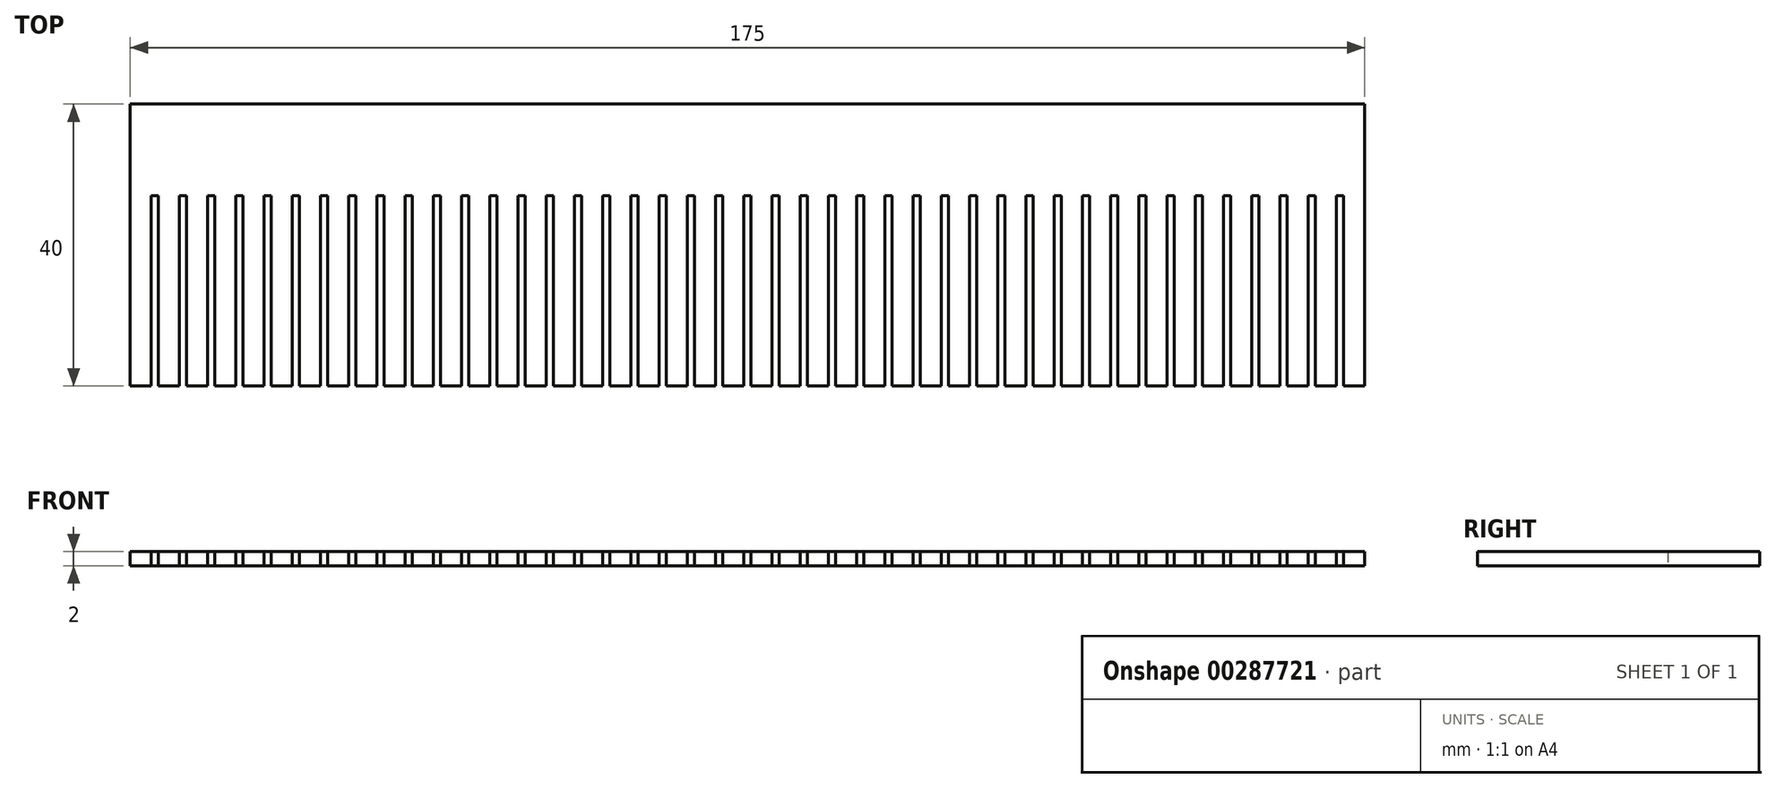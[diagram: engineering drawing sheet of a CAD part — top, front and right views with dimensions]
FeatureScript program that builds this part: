
annotation { "Feature Type Name" : "Feature", "Feature Type Description" : "" }
export const myFeature = defineFeature(function(context is Context, id is Id, definition is map)
    precondition{}
    {
        {
            var Q0;
            Q0=qCreatedBy(makeId("Top.planeOp"),FACE);
            var sketch = newSketch(context, id + "F0", { "sketchPlane" : qUnion([Q0])});
            skLineSegment(sketch, "E0", {"start": v(-88.37, 37.55) * mm, "end": v(86.63, 37.55) * mm});
            skLineSegment(sketch, "E1", {"start": v(-88.37, 37.55) * mm, "end": v(-88.37, 24.55) * mm});
            skLineSegment(sketch, "E2", {"start": v(-88.37, 24.55) * mm, "end": v(86.63, 24.55) * mm});
            skLineSegment(sketch, "E3", {"start": v(86.63, 24.55) * mm, "end": v(86.63, 37.55) * mm});
            skLineSegment(sketch, "E4", {"start": v(-88.37, 24.55) * mm, "end": v(-88.37, -2.45) * mm});
            skLineSegment(sketch, "E5", {"start": v(-88.37, -2.45) * mm, "end": v(-85.37, -2.45) * mm});
            skLineSegment(sketch, "E6", {"start": v(-85.37, -2.45) * mm, "end": v(-85.37, 24.55) * mm});
            skLineSegment(sketch, "E7.1.0.0", {"start": v(-81.37, -2.45) * mm, "end": v(-81.37, 24.55) * mm});
            skLineSegment(sketch, "E7.1.0.1", {"start": v(-84.37, 24.55) * mm, "end": v(-84.37, -2.45) * mm});
            skLineSegment(sketch, "E7.1.0.2", {"start": v(-84.37, -2.45) * mm, "end": v(-81.37, -2.45) * mm});
            skLineSegment(sketch, "E7.2.0.0", {"start": v(-77.37, -2.45) * mm, "end": v(-77.37, 24.55) * mm});
            skLineSegment(sketch, "E7.2.0.1", {"start": v(-80.37, 24.55) * mm, "end": v(-80.37, -2.45) * mm});
            skLineSegment(sketch, "E7.2.0.2", {"start": v(-80.37, -2.45) * mm, "end": v(-77.37, -2.45) * mm});
            skLineSegment(sketch, "E7.3.0.0", {"start": v(-73.37, -2.45) * mm, "end": v(-73.37, 24.55) * mm});
            skLineSegment(sketch, "E7.3.0.1", {"start": v(-76.37, 24.55) * mm, "end": v(-76.37, -2.45) * mm});
            skLineSegment(sketch, "E7.3.0.2", {"start": v(-76.37, -2.45) * mm, "end": v(-73.37, -2.45) * mm});
            skLineSegment(sketch, "E7.4.0.0", {"start": v(-69.37, -2.45) * mm, "end": v(-69.37, 24.55) * mm});
            skLineSegment(sketch, "E7.4.0.1", {"start": v(-72.37, 24.55) * mm, "end": v(-72.37, -2.45) * mm});
            skLineSegment(sketch, "E7.4.0.2", {"start": v(-72.37, -2.45) * mm, "end": v(-69.37, -2.45) * mm});
            skLineSegment(sketch, "E7.5.0.0", {"start": v(-65.37, -2.45) * mm, "end": v(-65.37, 24.55) * mm});
            skLineSegment(sketch, "E7.5.0.1", {"start": v(-68.37, 24.55) * mm, "end": v(-68.37, -2.45) * mm});
            skLineSegment(sketch, "E7.5.0.2", {"start": v(-68.37, -2.45) * mm, "end": v(-65.37, -2.45) * mm});
            skLineSegment(sketch, "E7.6.0.0", {"start": v(-61.37, -2.45) * mm, "end": v(-61.37, 24.55) * mm});
            skLineSegment(sketch, "E7.6.0.1", {"start": v(-64.37, 24.55) * mm, "end": v(-64.37, -2.45) * mm});
            skLineSegment(sketch, "E7.6.0.2", {"start": v(-64.37, -2.45) * mm, "end": v(-61.37, -2.45) * mm});
            skLineSegment(sketch, "E7.7.0.0", {"start": v(-57.37, -2.45) * mm, "end": v(-57.37, 24.55) * mm});
            skLineSegment(sketch, "E7.7.0.1", {"start": v(-60.37, 24.55) * mm, "end": v(-60.37, -2.45) * mm});
            skLineSegment(sketch, "E7.7.0.2", {"start": v(-60.37, -2.45) * mm, "end": v(-57.37, -2.45) * mm});
            skLineSegment(sketch, "E7.8.0.0", {"start": v(-53.37, -2.45) * mm, "end": v(-53.37, 24.55) * mm});
            skLineSegment(sketch, "E7.8.0.1", {"start": v(-56.37, 24.55) * mm, "end": v(-56.37, -2.45) * mm});
            skLineSegment(sketch, "E7.8.0.2", {"start": v(-56.37, -2.45) * mm, "end": v(-53.37, -2.45) * mm});
            skLineSegment(sketch, "E7.9.0.0", {"start": v(-49.37, -2.45) * mm, "end": v(-49.37, 24.55) * mm});
            skLineSegment(sketch, "E7.9.0.1", {"start": v(-52.37, 24.55) * mm, "end": v(-52.37, -2.45) * mm});
            skLineSegment(sketch, "E7.9.0.2", {"start": v(-52.37, -2.45) * mm, "end": v(-49.37, -2.45) * mm});
            skLineSegment(sketch, "E7.10.0.0", {"start": v(-45.37, -2.45) * mm, "end": v(-45.37, 24.55) * mm});
            skLineSegment(sketch, "E7.10.0.1", {"start": v(-48.37, 24.55) * mm, "end": v(-48.37, -2.45) * mm});
            skLineSegment(sketch, "E7.10.0.2", {"start": v(-48.37, -2.45) * mm, "end": v(-45.37, -2.45) * mm});
            skLineSegment(sketch, "E7.11.0.0", {"start": v(-41.37, -2.45) * mm, "end": v(-41.37, 24.55) * mm});
            skLineSegment(sketch, "E7.11.0.1", {"start": v(-44.37, 24.55) * mm, "end": v(-44.37, -2.45) * mm});
            skLineSegment(sketch, "E7.11.0.2", {"start": v(-44.37, -2.45) * mm, "end": v(-41.37, -2.45) * mm});
            skLineSegment(sketch, "E7.12.0.0", {"start": v(-37.37, -2.45) * mm, "end": v(-37.37, 24.55) * mm});
            skLineSegment(sketch, "E7.12.0.1", {"start": v(-40.37, 24.55) * mm, "end": v(-40.37, -2.45) * mm});
            skLineSegment(sketch, "E7.12.0.2", {"start": v(-40.37, -2.45) * mm, "end": v(-37.37, -2.45) * mm});
            skLineSegment(sketch, "E7.13.0.0", {"start": v(-33.37, -2.45) * mm, "end": v(-33.37, 24.55) * mm});
            skLineSegment(sketch, "E7.13.0.1", {"start": v(-36.37, 24.55) * mm, "end": v(-36.37, -2.45) * mm});
            skLineSegment(sketch, "E7.13.0.2", {"start": v(-36.37, -2.45) * mm, "end": v(-33.37, -2.45) * mm});
            skLineSegment(sketch, "E7.14.0.0", {"start": v(-29.37, -2.45) * mm, "end": v(-29.37, 24.55) * mm});
            skLineSegment(sketch, "E7.14.0.1", {"start": v(-32.37, 24.55) * mm, "end": v(-32.37, -2.45) * mm});
            skLineSegment(sketch, "E7.14.0.2", {"start": v(-32.37, -2.45) * mm, "end": v(-29.37, -2.45) * mm});
            skLineSegment(sketch, "E7.15.0.0", {"start": v(-25.37, -2.45) * mm, "end": v(-25.37, 24.55) * mm});
            skLineSegment(sketch, "E7.15.0.1", {"start": v(-28.37, 24.55) * mm, "end": v(-28.37, -2.45) * mm});
            skLineSegment(sketch, "E7.15.0.2", {"start": v(-28.37, -2.45) * mm, "end": v(-25.37, -2.45) * mm});
            skLineSegment(sketch, "E7.16.0.0", {"start": v(-21.37, -2.45) * mm, "end": v(-21.37, 24.55) * mm});
            skLineSegment(sketch, "E7.16.0.1", {"start": v(-24.37, 24.55) * mm, "end": v(-24.37, -2.45) * mm});
            skLineSegment(sketch, "E7.16.0.2", {"start": v(-24.37, -2.45) * mm, "end": v(-21.37, -2.45) * mm});
            skLineSegment(sketch, "E7.17.0.0", {"start": v(-17.37, -2.45) * mm, "end": v(-17.37, 24.55) * mm});
            skLineSegment(sketch, "E7.17.0.1", {"start": v(-20.37, 24.55) * mm, "end": v(-20.37, -2.45) * mm});
            skLineSegment(sketch, "E7.17.0.2", {"start": v(-20.37, -2.45) * mm, "end": v(-17.37, -2.45) * mm});
            skLineSegment(sketch, "E7.18.0.0", {"start": v(-13.37, -2.45) * mm, "end": v(-13.37, 24.55) * mm});
            skLineSegment(sketch, "E7.18.0.1", {"start": v(-16.37, 24.55) * mm, "end": v(-16.37, -2.45) * mm});
            skLineSegment(sketch, "E7.18.0.2", {"start": v(-16.37, -2.45) * mm, "end": v(-13.37, -2.45) * mm});
            skLineSegment(sketch, "E7.19.0.0", {"start": v(-9.37, -2.45) * mm, "end": v(-9.37, 24.55) * mm});
            skLineSegment(sketch, "E7.19.0.1", {"start": v(-12.37, 24.55) * mm, "end": v(-12.37, -2.45) * mm});
            skLineSegment(sketch, "E7.19.0.2", {"start": v(-12.37, -2.45) * mm, "end": v(-9.37, -2.45) * mm});
            skLineSegment(sketch, "E7.20.0.0", {"start": v(-5.37, -2.45) * mm, "end": v(-5.37, 24.55) * mm});
            skLineSegment(sketch, "E7.20.0.1", {"start": v(-8.37, 24.55) * mm, "end": v(-8.37, -2.45) * mm});
            skLineSegment(sketch, "E7.20.0.2", {"start": v(-8.37, -2.45) * mm, "end": v(-5.37, -2.45) * mm});
            skLineSegment(sketch, "E7.21.0.0", {"start": v(-1.37, -2.45) * mm, "end": v(-1.37, 24.55) * mm});
            skLineSegment(sketch, "E7.21.0.1", {"start": v(-4.37, 24.55) * mm, "end": v(-4.37, -2.45) * mm});
            skLineSegment(sketch, "E7.21.0.2", {"start": v(-4.37, -2.45) * mm, "end": v(-1.37, -2.45) * mm});
            skLineSegment(sketch, "E7.22.0.0", {"start": v(2.63, -2.45) * mm, "end": v(2.63, 24.55) * mm});
            skLineSegment(sketch, "E7.22.0.1", {"start": v(-0.37, 24.55) * mm, "end": v(-0.37, -2.45) * mm});
            skLineSegment(sketch, "E7.22.0.2", {"start": v(-0.37, -2.45) * mm, "end": v(2.63, -2.45) * mm});
            skLineSegment(sketch, "E7.23.0.0", {"start": v(6.63, -2.45) * mm, "end": v(6.63, 24.55) * mm});
            skLineSegment(sketch, "E7.23.0.1", {"start": v(3.63, 24.55) * mm, "end": v(3.63, -2.45) * mm});
            skLineSegment(sketch, "E7.23.0.2", {"start": v(3.63, -2.45) * mm, "end": v(6.63, -2.45) * mm});
            skLineSegment(sketch, "E7.24.0.0", {"start": v(10.63, -2.45) * mm, "end": v(10.63, 24.55) * mm});
            skLineSegment(sketch, "E7.24.0.1", {"start": v(7.63, 24.55) * mm, "end": v(7.63, -2.45) * mm});
            skLineSegment(sketch, "E7.24.0.2", {"start": v(7.63, -2.45) * mm, "end": v(10.63, -2.45) * mm});
            skLineSegment(sketch, "E7.25.0.0", {"start": v(14.63, -2.45) * mm, "end": v(14.63, 24.55) * mm});
            skLineSegment(sketch, "E7.25.0.1", {"start": v(11.63, 24.55) * mm, "end": v(11.63, -2.45) * mm});
            skLineSegment(sketch, "E7.25.0.2", {"start": v(11.63, -2.45) * mm, "end": v(14.63, -2.45) * mm});
            skLineSegment(sketch, "E7.26.0.0", {"start": v(18.63, -2.45) * mm, "end": v(18.63, 24.55) * mm});
            skLineSegment(sketch, "E7.26.0.1", {"start": v(15.63, 24.55) * mm, "end": v(15.63, -2.45) * mm});
            skLineSegment(sketch, "E7.26.0.2", {"start": v(15.63, -2.45) * mm, "end": v(18.63, -2.45) * mm});
            skLineSegment(sketch, "E7.27.0.0", {"start": v(22.63, -2.45) * mm, "end": v(22.63, 24.55) * mm});
            skLineSegment(sketch, "E7.27.0.1", {"start": v(19.63, 24.55) * mm, "end": v(19.63, -2.45) * mm});
            skLineSegment(sketch, "E7.27.0.2", {"start": v(19.63, -2.45) * mm, "end": v(22.63, -2.45) * mm});
            skLineSegment(sketch, "E7.28.0.0", {"start": v(26.63, -2.45) * mm, "end": v(26.63, 24.55) * mm});
            skLineSegment(sketch, "E7.28.0.1", {"start": v(23.63, 24.55) * mm, "end": v(23.63, -2.45) * mm});
            skLineSegment(sketch, "E7.28.0.2", {"start": v(23.63, -2.45) * mm, "end": v(26.63, -2.45) * mm});
            skLineSegment(sketch, "E7.29.0.0", {"start": v(30.63, -2.45) * mm, "end": v(30.63, 24.55) * mm});
            skLineSegment(sketch, "E7.29.0.1", {"start": v(27.63, 24.55) * mm, "end": v(27.63, -2.45) * mm});
            skLineSegment(sketch, "E7.29.0.2", {"start": v(27.63, -2.45) * mm, "end": v(30.63, -2.45) * mm});
            skLineSegment(sketch, "E7.30.0.0", {"start": v(34.63, -2.45) * mm, "end": v(34.63, 24.55) * mm});
            skLineSegment(sketch, "E7.30.0.1", {"start": v(31.63, 24.55) * mm, "end": v(31.63, -2.45) * mm});
            skLineSegment(sketch, "E7.30.0.2", {"start": v(31.63, -2.45) * mm, "end": v(34.63, -2.45) * mm});
            skLineSegment(sketch, "E7.31.0.0", {"start": v(38.63, -2.45) * mm, "end": v(38.63, 24.55) * mm});
            skLineSegment(sketch, "E7.31.0.1", {"start": v(35.63, 24.55) * mm, "end": v(35.63, -2.45) * mm});
            skLineSegment(sketch, "E7.31.0.2", {"start": v(35.63, -2.45) * mm, "end": v(38.63, -2.45) * mm});
            skLineSegment(sketch, "E7.32.0.0", {"start": v(42.63, -2.45) * mm, "end": v(42.63, 24.55) * mm});
            skLineSegment(sketch, "E7.32.0.1", {"start": v(39.63, 24.55) * mm, "end": v(39.63, -2.45) * mm});
            skLineSegment(sketch, "E7.32.0.2", {"start": v(39.63, -2.45) * mm, "end": v(42.63, -2.45) * mm});
            skLineSegment(sketch, "E7.33.0.0", {"start": v(46.63, -2.45) * mm, "end": v(46.63, 24.55) * mm});
            skLineSegment(sketch, "E7.33.0.1", {"start": v(43.63, 24.55) * mm, "end": v(43.63, -2.45) * mm});
            skLineSegment(sketch, "E7.33.0.2", {"start": v(43.63, -2.45) * mm, "end": v(46.63, -2.45) * mm});
            skLineSegment(sketch, "E7.34.0.0", {"start": v(50.63, -2.45) * mm, "end": v(50.63, 24.55) * mm});
            skLineSegment(sketch, "E7.34.0.1", {"start": v(47.63, 24.55) * mm, "end": v(47.63, -2.45) * mm});
            skLineSegment(sketch, "E7.34.0.2", {"start": v(47.63, -2.45) * mm, "end": v(50.63, -2.45) * mm});
            skLineSegment(sketch, "E7.35.0.0", {"start": v(54.63, -2.45) * mm, "end": v(54.63, 24.55) * mm});
            skLineSegment(sketch, "E7.35.0.1", {"start": v(51.63, 24.55) * mm, "end": v(51.63, -2.45) * mm});
            skLineSegment(sketch, "E7.35.0.2", {"start": v(51.63, -2.45) * mm, "end": v(54.63, -2.45) * mm});
            skLineSegment(sketch, "E7.36.0.0", {"start": v(58.63, -2.45) * mm, "end": v(58.63, 24.55) * mm});
            skLineSegment(sketch, "E7.36.0.1", {"start": v(55.63, 24.55) * mm, "end": v(55.63, -2.45) * mm});
            skLineSegment(sketch, "E7.36.0.2", {"start": v(55.63, -2.45) * mm, "end": v(58.63, -2.45) * mm});
            skLineSegment(sketch, "E7.37.0.0", {"start": v(62.63, -2.45) * mm, "end": v(62.63, 24.55) * mm});
            skLineSegment(sketch, "E7.37.0.1", {"start": v(59.63, 24.55) * mm, "end": v(59.63, -2.45) * mm});
            skLineSegment(sketch, "E7.37.0.2", {"start": v(59.63, -2.45) * mm, "end": v(62.63, -2.45) * mm});
            skLineSegment(sketch, "E7.38.0.0", {"start": v(66.63, -2.45) * mm, "end": v(66.63, 24.55) * mm});
            skLineSegment(sketch, "E7.38.0.1", {"start": v(63.63, 24.55) * mm, "end": v(63.63, -2.45) * mm});
            skLineSegment(sketch, "E7.38.0.2", {"start": v(63.63, -2.45) * mm, "end": v(66.63, -2.45) * mm});
            skLineSegment(sketch, "E7.39.0.0", {"start": v(70.63, -2.45) * mm, "end": v(70.63, 24.55) * mm});
            skLineSegment(sketch, "E7.39.0.1", {"start": v(67.63, 24.55) * mm, "end": v(67.63, -2.45) * mm});
            skLineSegment(sketch, "E7.39.0.2", {"start": v(67.63, -2.45) * mm, "end": v(70.63, -2.45) * mm});
            skLineSegment(sketch, "E7.40.0.0", {"start": v(74.63, -2.45) * mm, "end": v(74.63, 24.55) * mm});
            skLineSegment(sketch, "E7.40.0.1", {"start": v(71.63, 24.55) * mm, "end": v(71.63, -2.45) * mm});
            skLineSegment(sketch, "E7.40.0.2", {"start": v(71.63, -2.45) * mm, "end": v(74.63, -2.45) * mm});
            skLineSegment(sketch, "E7.41.0.0", {"start": v(78.63, -2.45) * mm, "end": v(78.63, 24.55) * mm});
            skLineSegment(sketch, "E7.41.0.1", {"start": v(75.63, 24.55) * mm, "end": v(75.63, -2.45) * mm});
            skLineSegment(sketch, "E7.41.0.2", {"start": v(75.63, -2.45) * mm, "end": v(78.63, -2.45) * mm});
            skLineSegment(sketch, "E7.42.0.0", {"start": v(82.63, -2.45) * mm, "end": v(82.63, 24.55) * mm});
            skLineSegment(sketch, "E7.42.0.1", {"start": v(79.63, 24.55) * mm, "end": v(79.63, -2.45) * mm});
            skLineSegment(sketch, "E7.42.0.2", {"start": v(79.63, -2.45) * mm, "end": v(82.63, -2.45) * mm});
            skLineSegment(sketch, "E7.43.0.0", {"start": v(86.63, -2.45) * mm, "end": v(86.63, 24.55) * mm});
            skLineSegment(sketch, "E7.43.0.1", {"start": v(83.63, 24.55) * mm, "end": v(83.63, -2.45) * mm});
            skLineSegment(sketch, "E7.43.0.2", {"start": v(83.63, -2.45) * mm, "end": v(86.63, -2.45) * mm});
            skLineSegment(sketch, "E7.direction1", {"start": v(-85.37, -2.45) * mm, "end": v(-81.37, -2.45) * mm, "construction": true});
            skSolve(sketch);
        }
        {
            var Q0;
            {var subQ0=sQuery(id+"F0.wireOp",EDGE,"E4");Q0=makeQuery(id+"F0.imprint","IMPRINT",FACE,{"disambiguationData":[TD([[makeQuery(id+"F0.imprint","IMPRINT",EDGE,{"derivedFrom":subQ0}),1.0]])]});}
            var Q1;
            {var subQ0=sQuery(id+"F0.wireOp",EDGE,"E7.1.0.0");Q1=makeQuery(id+"F0.imprint","IMPRINT",FACE,{"disambiguationData":[TD([[makeQuery(id+"F0.imprint","IMPRINT",EDGE,{"derivedFrom":subQ0}),1.0]])]});}
            var Q2;
            {var subQ0=sQuery(id+"F0.wireOp",EDGE,"E7.2.0.0");Q2=makeQuery(id+"F0.imprint","IMPRINT",FACE,{"disambiguationData":[TD([[makeQuery(id+"F0.imprint","IMPRINT",EDGE,{"derivedFrom":subQ0}),1.0]])]});}
            var Q3;
            {var subQ0=sQuery(id+"F0.wireOp",EDGE,"E7.3.0.0");Q3=makeQuery(id+"F0.imprint","IMPRINT",FACE,{"disambiguationData":[TD([[makeQuery(id+"F0.imprint","IMPRINT",EDGE,{"derivedFrom":subQ0}),1.0]])]});}
            var Q4;
            {var subQ0=sQuery(id+"F0.wireOp",EDGE,"E7.4.0.0");Q4=makeQuery(id+"F0.imprint","IMPRINT",FACE,{"disambiguationData":[TD([[makeQuery(id+"F0.imprint","IMPRINT",EDGE,{"derivedFrom":subQ0}),1.0]])]});}
            var Q5;
            {var subQ0=sQuery(id+"F0.wireOp",EDGE,"E7.5.0.0");Q5=makeQuery(id+"F0.imprint","IMPRINT",FACE,{"disambiguationData":[TD([[makeQuery(id+"F0.imprint","IMPRINT",EDGE,{"derivedFrom":subQ0}),1.0]])]});}
            var Q6;
            {var subQ0=sQuery(id+"F0.wireOp",EDGE,"E7.6.0.0");Q6=makeQuery(id+"F0.imprint","IMPRINT",FACE,{"disambiguationData":[TD([[makeQuery(id+"F0.imprint","IMPRINT",EDGE,{"derivedFrom":subQ0}),1.0]])]});}
            var Q7;
            {var subQ0=sQuery(id+"F0.wireOp",EDGE,"E7.7.0.0");Q7=makeQuery(id+"F0.imprint","IMPRINT",FACE,{"disambiguationData":[TD([[makeQuery(id+"F0.imprint","IMPRINT",EDGE,{"derivedFrom":subQ0}),1.0]])]});}
            var Q8;
            {var subQ0=sQuery(id+"F0.wireOp",EDGE,"E7.8.0.0");Q8=makeQuery(id+"F0.imprint","IMPRINT",FACE,{"disambiguationData":[TD([[makeQuery(id+"F0.imprint","IMPRINT",EDGE,{"derivedFrom":subQ0}),1.0]])]});}
            var Q9;
            {var subQ0=sQuery(id+"F0.wireOp",EDGE,"E7.9.0.0");Q9=makeQuery(id+"F0.imprint","IMPRINT",FACE,{"disambiguationData":[TD([[makeQuery(id+"F0.imprint","IMPRINT",EDGE,{"derivedFrom":subQ0}),1.0]])]});}
            var Q10;
            {var subQ0=sQuery(id+"F0.wireOp",EDGE,"E7.10.0.0");Q10=makeQuery(id+"F0.imprint","IMPRINT",FACE,{"disambiguationData":[TD([[makeQuery(id+"F0.imprint","IMPRINT",EDGE,{"derivedFrom":subQ0}),1.0]])]});}
            var Q11;
            {var subQ0=sQuery(id+"F0.wireOp",EDGE,"E7.11.0.0");Q11=makeQuery(id+"F0.imprint","IMPRINT",FACE,{"disambiguationData":[TD([[makeQuery(id+"F0.imprint","IMPRINT",EDGE,{"derivedFrom":subQ0}),1.0]])]});}
            var Q12;
            {var subQ0=sQuery(id+"F0.wireOp",EDGE,"E7.12.0.0");Q12=makeQuery(id+"F0.imprint","IMPRINT",FACE,{"disambiguationData":[TD([[makeQuery(id+"F0.imprint","IMPRINT",EDGE,{"derivedFrom":subQ0}),1.0]])]});}
            var Q13;
            {var subQ0=sQuery(id+"F0.wireOp",EDGE,"E7.13.0.0");Q13=makeQuery(id+"F0.imprint","IMPRINT",FACE,{"disambiguationData":[TD([[makeQuery(id+"F0.imprint","IMPRINT",EDGE,{"derivedFrom":subQ0}),1.0]])]});}
            var Q14;
            {var subQ0=sQuery(id+"F0.wireOp",EDGE,"E7.14.0.0");Q14=makeQuery(id+"F0.imprint","IMPRINT",FACE,{"disambiguationData":[TD([[makeQuery(id+"F0.imprint","IMPRINT",EDGE,{"derivedFrom":subQ0}),1.0]])]});}
            var Q15;
            {var subQ0=sQuery(id+"F0.wireOp",EDGE,"E7.15.0.0");Q15=makeQuery(id+"F0.imprint","IMPRINT",FACE,{"disambiguationData":[TD([[makeQuery(id+"F0.imprint","IMPRINT",EDGE,{"derivedFrom":subQ0}),1.0]])]});}
            var Q16;
            {var subQ0=sQuery(id+"F0.wireOp",EDGE,"E7.16.0.0");Q16=makeQuery(id+"F0.imprint","IMPRINT",FACE,{"disambiguationData":[TD([[makeQuery(id+"F0.imprint","IMPRINT",EDGE,{"derivedFrom":subQ0}),1.0]])]});}
            var Q17;
            {var subQ0=sQuery(id+"F0.wireOp",EDGE,"E7.17.0.0");Q17=makeQuery(id+"F0.imprint","IMPRINT",FACE,{"disambiguationData":[TD([[makeQuery(id+"F0.imprint","IMPRINT",EDGE,{"derivedFrom":subQ0}),1.0]])]});}
            var Q18;
            {var subQ0=sQuery(id+"F0.wireOp",EDGE,"E7.18.0.0");Q18=makeQuery(id+"F0.imprint","IMPRINT",FACE,{"disambiguationData":[TD([[makeQuery(id+"F0.imprint","IMPRINT",EDGE,{"derivedFrom":subQ0}),1.0]])]});}
            var Q19;
            {var subQ0=sQuery(id+"F0.wireOp",EDGE,"E7.19.0.0");Q19=makeQuery(id+"F0.imprint","IMPRINT",FACE,{"disambiguationData":[TD([[makeQuery(id+"F0.imprint","IMPRINT",EDGE,{"derivedFrom":subQ0}),1.0]])]});}
            var Q20;
            {var subQ0=sQuery(id+"F0.wireOp",EDGE,"E7.20.0.0");Q20=makeQuery(id+"F0.imprint","IMPRINT",FACE,{"disambiguationData":[TD([[makeQuery(id+"F0.imprint","IMPRINT",EDGE,{"derivedFrom":subQ0}),1.0]])]});}
            var Q21;
            {var subQ0=sQuery(id+"F0.wireOp",EDGE,"E7.21.0.0");Q21=makeQuery(id+"F0.imprint","IMPRINT",FACE,{"disambiguationData":[TD([[makeQuery(id+"F0.imprint","IMPRINT",EDGE,{"derivedFrom":subQ0}),1.0]])]});}
            var Q22;
            {var subQ0=sQuery(id+"F0.wireOp",EDGE,"E7.22.0.0");Q22=makeQuery(id+"F0.imprint","IMPRINT",FACE,{"disambiguationData":[TD([[makeQuery(id+"F0.imprint","IMPRINT",EDGE,{"derivedFrom":subQ0}),1.0]])]});}
            var Q23;
            {var subQ0=sQuery(id+"F0.wireOp",EDGE,"E7.23.0.0");Q23=makeQuery(id+"F0.imprint","IMPRINT",FACE,{"disambiguationData":[TD([[makeQuery(id+"F0.imprint","IMPRINT",EDGE,{"derivedFrom":subQ0}),1.0]])]});}
            var Q24;
            {var subQ0=sQuery(id+"F0.wireOp",EDGE,"E7.24.0.0");Q24=makeQuery(id+"F0.imprint","IMPRINT",FACE,{"disambiguationData":[TD([[makeQuery(id+"F0.imprint","IMPRINT",EDGE,{"derivedFrom":subQ0}),1.0]])]});}
            var Q25;
            {var subQ0=sQuery(id+"F0.wireOp",EDGE,"E7.25.0.0");Q25=makeQuery(id+"F0.imprint","IMPRINT",FACE,{"disambiguationData":[TD([[makeQuery(id+"F0.imprint","IMPRINT",EDGE,{"derivedFrom":subQ0}),1.0]])]});}
            var Q26;
            {var subQ0=sQuery(id+"F0.wireOp",EDGE,"E7.26.0.0");Q26=makeQuery(id+"F0.imprint","IMPRINT",FACE,{"disambiguationData":[TD([[makeQuery(id+"F0.imprint","IMPRINT",EDGE,{"derivedFrom":subQ0}),1.0]])]});}
            var Q27;
            {var subQ0=sQuery(id+"F0.wireOp",EDGE,"E7.27.0.0");Q27=makeQuery(id+"F0.imprint","IMPRINT",FACE,{"disambiguationData":[TD([[makeQuery(id+"F0.imprint","IMPRINT",EDGE,{"derivedFrom":subQ0}),1.0]])]});}
            var Q28;
            {var subQ0=sQuery(id+"F0.wireOp",EDGE,"E7.28.0.0");Q28=makeQuery(id+"F0.imprint","IMPRINT",FACE,{"disambiguationData":[TD([[makeQuery(id+"F0.imprint","IMPRINT",EDGE,{"derivedFrom":subQ0}),1.0]])]});}
            var Q29;
            {var subQ0=sQuery(id+"F0.wireOp",EDGE,"E7.29.0.0");Q29=makeQuery(id+"F0.imprint","IMPRINT",FACE,{"disambiguationData":[TD([[makeQuery(id+"F0.imprint","IMPRINT",EDGE,{"derivedFrom":subQ0}),1.0]])]});}
            var Q30;
            {var subQ0=sQuery(id+"F0.wireOp",EDGE,"E7.30.0.0");Q30=makeQuery(id+"F0.imprint","IMPRINT",FACE,{"disambiguationData":[TD([[makeQuery(id+"F0.imprint","IMPRINT",EDGE,{"derivedFrom":subQ0}),1.0]])]});}
            var Q31;
            {var subQ0=sQuery(id+"F0.wireOp",EDGE,"E7.31.0.0");Q31=makeQuery(id+"F0.imprint","IMPRINT",FACE,{"disambiguationData":[TD([[makeQuery(id+"F0.imprint","IMPRINT",EDGE,{"derivedFrom":subQ0}),1.0]])]});}
            var Q32;
            {var subQ0=sQuery(id+"F0.wireOp",EDGE,"E7.32.0.0");Q32=makeQuery(id+"F0.imprint","IMPRINT",FACE,{"disambiguationData":[TD([[makeQuery(id+"F0.imprint","IMPRINT",EDGE,{"derivedFrom":subQ0}),1.0]])]});}
            var Q33;
            {var subQ0=sQuery(id+"F0.wireOp",EDGE,"E7.33.0.0");Q33=makeQuery(id+"F0.imprint","IMPRINT",FACE,{"disambiguationData":[TD([[makeQuery(id+"F0.imprint","IMPRINT",EDGE,{"derivedFrom":subQ0}),1.0]])]});}
            var Q34;
            {var subQ0=sQuery(id+"F0.wireOp",EDGE,"E7.34.0.0");Q34=makeQuery(id+"F0.imprint","IMPRINT",FACE,{"disambiguationData":[TD([[makeQuery(id+"F0.imprint","IMPRINT",EDGE,{"derivedFrom":subQ0}),1.0]])]});}
            var Q35;
            {var subQ0=sQuery(id+"F0.wireOp",EDGE,"E7.35.0.0");Q35=makeQuery(id+"F0.imprint","IMPRINT",FACE,{"disambiguationData":[TD([[makeQuery(id+"F0.imprint","IMPRINT",EDGE,{"derivedFrom":subQ0}),1.0]])]});}
            var Q36;
            {var subQ0=sQuery(id+"F0.wireOp",EDGE,"E7.36.0.0");Q36=makeQuery(id+"F0.imprint","IMPRINT",FACE,{"disambiguationData":[TD([[makeQuery(id+"F0.imprint","IMPRINT",EDGE,{"derivedFrom":subQ0}),1.0]])]});}
            var Q37;
            {var subQ0=sQuery(id+"F0.wireOp",EDGE,"E7.37.0.0");Q37=makeQuery(id+"F0.imprint","IMPRINT",FACE,{"disambiguationData":[TD([[makeQuery(id+"F0.imprint","IMPRINT",EDGE,{"derivedFrom":subQ0}),1.0]])]});}
            var Q38;
            {var subQ0=sQuery(id+"F0.wireOp",EDGE,"E7.38.0.0");Q38=makeQuery(id+"F0.imprint","IMPRINT",FACE,{"disambiguationData":[TD([[makeQuery(id+"F0.imprint","IMPRINT",EDGE,{"derivedFrom":subQ0}),1.0]])]});}
            var Q39;
            {var subQ0=sQuery(id+"F0.wireOp",EDGE,"E7.39.0.0");Q39=makeQuery(id+"F0.imprint","IMPRINT",FACE,{"disambiguationData":[TD([[makeQuery(id+"F0.imprint","IMPRINT",EDGE,{"derivedFrom":subQ0}),1.0]])]});}
            var Q40;
            {var subQ0=sQuery(id+"F0.wireOp",EDGE,"E7.40.0.0");Q40=makeQuery(id+"F0.imprint","IMPRINT",FACE,{"disambiguationData":[TD([[makeQuery(id+"F0.imprint","IMPRINT",EDGE,{"derivedFrom":subQ0}),1.0]])]});}
            var Q41;
            {var subQ0=sQuery(id+"F0.wireOp",EDGE,"E7.41.0.0");Q41=makeQuery(id+"F0.imprint","IMPRINT",FACE,{"disambiguationData":[TD([[makeQuery(id+"F0.imprint","IMPRINT",EDGE,{"derivedFrom":subQ0}),1.0]])]});}
            var Q42;
            {var subQ0=sQuery(id+"F0.wireOp",EDGE,"E7.42.0.0");Q42=makeQuery(id+"F0.imprint","IMPRINT",FACE,{"disambiguationData":[TD([[makeQuery(id+"F0.imprint","IMPRINT",EDGE,{"derivedFrom":subQ0}),1.0]])]});}
            var Q43;
            {var subQ0=sQuery(id+"F0.wireOp",EDGE,"E7.43.0.0");Q43=makeQuery(id+"F0.imprint","IMPRINT",FACE,{"disambiguationData":[TD([[makeQuery(id+"F0.imprint","IMPRINT",EDGE,{"derivedFrom":subQ0}),1.0]])]});}
            var Q44;
            Q44=makeQuery(id+"F0.imprint","IMPRINT",FACE,{"disambiguationData":[TD([[makeQuery(id+"F0.imprint","IMPRINT",EDGE,{"derivedFrom":sQuery(id+"F0.wireOp",EDGE,"E0")}),-1.0]])]});
            extrude(context, id + "F1", {"entities" : qUnion([Q0, Q1, Q2, Q3, Q4, Q5, Q6, Q7, Q8, Q9, Q10, Q11, Q12, Q13, Q14, Q15, Q16, Q17, Q18, Q19, Q20, Q21, Q22, Q23, Q24, Q25, Q26, Q27, Q28, Q29, Q30, Q31, Q32, Q33, Q34, Q35, Q36, Q37, Q38, Q39, Q40, Q41, Q42, Q43, Q44]), "depth" : 2 * mm});
        }
    });
